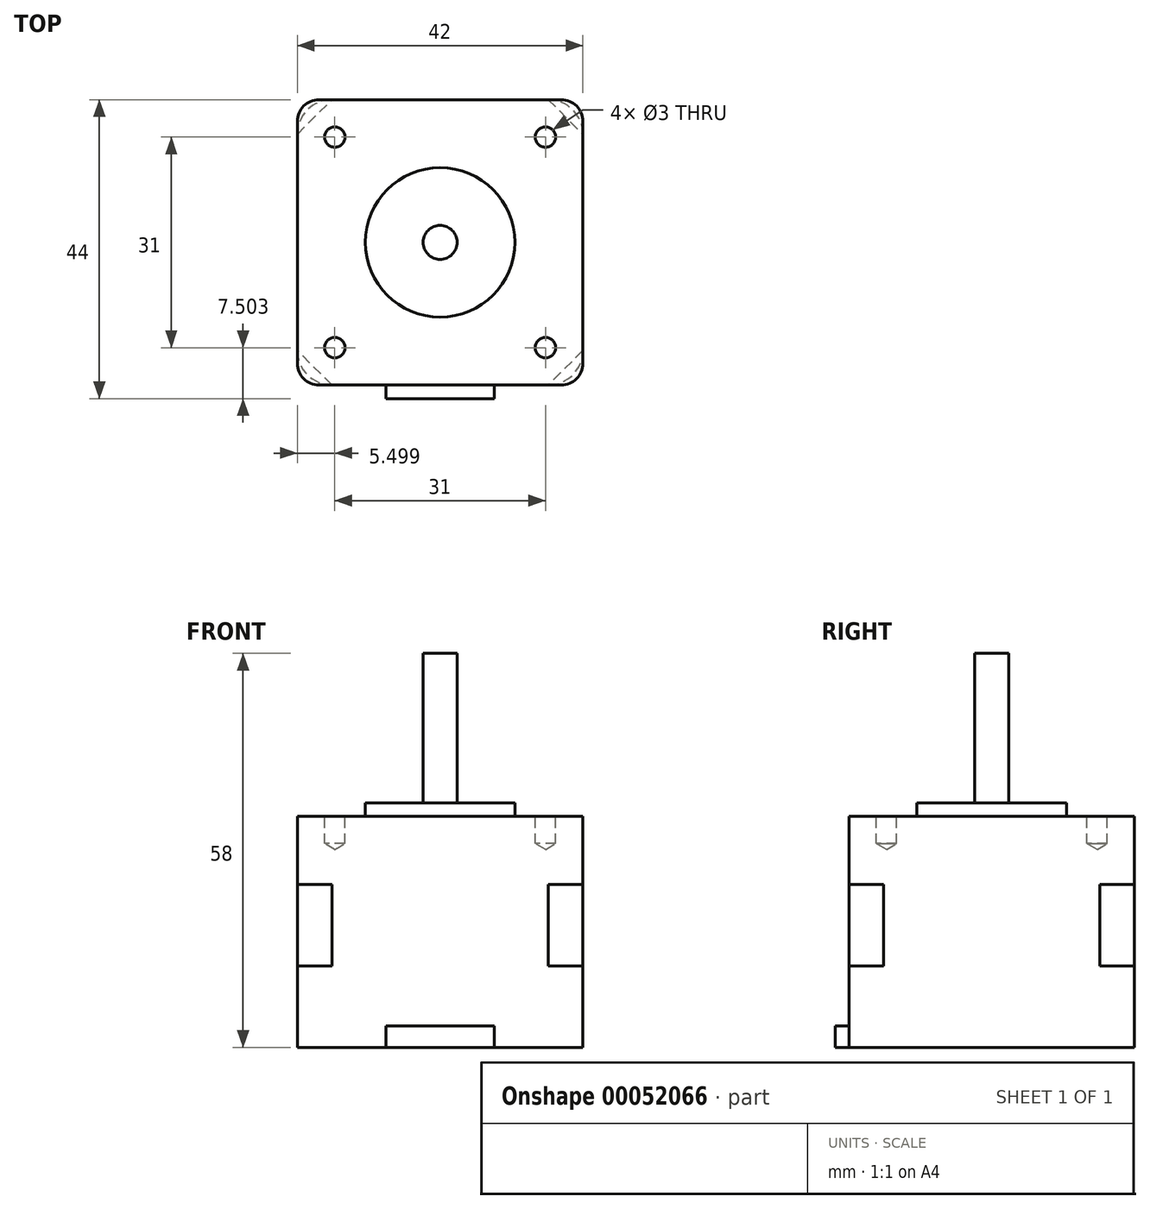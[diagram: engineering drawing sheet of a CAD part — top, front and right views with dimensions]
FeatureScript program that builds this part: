
annotation { "Feature Type Name" : "Feature", "Feature Type Description" : "" }
export const myFeature = defineFeature(function(context is Context, id is Id, definition is map)
    precondition{}
    {
        {
            var Q0;
            Q0=qCreatedBy(makeId("Top.planeOp"),FACE);
            var sketch = newSketch(context, id + "F0", { "sketchPlane" : qUnion([Q0])});
            skLineSegment(sketch, "E0.bottom", {"start": v(-20.04, 16.68) * mm, "end": v(21.96, 16.68) * mm});
            skLineSegment(sketch, "E0.top", {"start": v(-20.04, -25.32) * mm, "end": v(21.96, -25.32) * mm});
            skLineSegment(sketch, "E0.left", {"start": v(-20.04, 16.68) * mm, "end": v(-20.04, -25.32) * mm});
            skLineSegment(sketch, "E0.right", {"start": v(21.96, 16.68) * mm, "end": v(21.96, -25.32) * mm});
            skSolve(sketch);
        }
        {
            var Q0;
            Q0=makeQuery(id+"F0.imprint","IMPRINT",FACE,{"disambiguationData":[TD([[makeQuery(id+"F0.imprint","IMPRINT",EDGE,{"derivedFrom":sQuery(id+"F0.wireOp",EDGE,"E0.bottom")}),-1.0]])]});
            extrude(context, id + "F1", {"entities" : qUnion([Q0]), "depth" : 10 * mm});
        }
        {
            var Q0;
            Q0=makeQuery(id+"F1.opExtrude","CAP_FACE",FACE,{"disambiguationData":[OSD([sQuery(id+"F0.wireOp",EDGE,"E0.bottom"),sQuery(id+"F0.wireOp",EDGE,"E0.top"),sQuery(id+"F0.wireOp",EDGE,"E0.left"),sQuery(id+"F0.wireOp",EDGE,"E0.right")])],"isStart":false});
            var sketch = newSketch(context, id + "F2", { "sketchPlane" : qUnion([Q0])});
            skLineSegment(sketch, "E1", {"start": v(-20.04, 16.68) * mm, "end": v(21.96, -25.32) * mm, "construction": true});
            skLineSegment(sketch, "E2", {"start": v(21.96, 16.68) * mm, "end": v(-20.04, -25.32) * mm, "construction": true});
            skCircle(sketch, "E3", {"center": v(0.96, -4.32) * mm, "radius": 11 * mm});
            skSolve(sketch);
        }
        {
            var Q0;
            Q0=makeQuery(id+"F2.imprint","IMPRINT",FACE,{"disambiguationData":[TD([[makeQuery(id+"F2.imprint","IMPRINT",EDGE,{"derivedFrom":sQuery(id+"F2.wireOp",EDGE,"E3")}),1.0]])]});
            extrude(context, id + "F3", {"entities" : qUnion([Q0]), "operationType" : NewBodyOperationType.ADD, "depth" : 2 * mm});
        }
        {
            var Q0;
            Q0=makeQuery(id+"F1.opExtrude","SWEPT_EDGE",EDGE,{"disambiguationData":[OSD([sQuery(id+"F0.wireOp",EDGE,"E0.top"),sQuery(id+"F0.wireOp",EDGE,"E0.right")])]});
            var Q1;
            Q1=makeQuery(id+"F1.opExtrude","SWEPT_EDGE",EDGE,{"disambiguationData":[OSD([sQuery(id+"F0.wireOp",EDGE,"E0.bottom"),sQuery(id+"F0.wireOp",EDGE,"E0.right")])]});
            var Q2;
            Q2=makeQuery(id+"F1.opExtrude","SWEPT_EDGE",EDGE,{"disambiguationData":[OSD([sQuery(id+"F0.wireOp",EDGE,"E0.bottom"),sQuery(id+"F0.wireOp",EDGE,"E0.left")])]});
            var Q3;
            Q3=makeQuery(id+"F1.opExtrude","SWEPT_EDGE",EDGE,{"disambiguationData":[OSD([sQuery(id+"F0.wireOp",EDGE,"E0.top"),sQuery(id+"F0.wireOp",EDGE,"E0.left")])]});
            fillet(context, id + "F4", {"entities" : qUnion([Q0, Q1, Q2, Q3]), "radius" : 3.17 * mm, "tangentPropagation" : true, "allowEdgeOverflow" : false});
        }
        {
            var Q0;
            Q0=makeQuery(id+"F1.opExtrude","CAP_FACE",FACE,{"disambiguationData":[OSD([sQuery(id+"F0.wireOp",EDGE,"E0.bottom"),sQuery(id+"F0.wireOp",EDGE,"E0.top"),sQuery(id+"F0.wireOp",EDGE,"E0.left"),sQuery(id+"F0.wireOp",EDGE,"E0.right")])],"isStart":true});
            var sketch = newSketch(context, id + "F5", { "sketchPlane" : qUnion([Q0])});
            skLineSegment(sketch, "E4", {"start": v(-20.04, -11.6) * mm, "end": v(-20.04, 20.24) * mm});
            skLineSegment(sketch, "E5", {"start": v(0.96, 25.32) * mm, "end": v(0.96, -16.68) * mm, "construction": true});
            skLineSegment(sketch, "E6", {"start": v(-14.96, 25.32) * mm, "end": v(0.96, 25.32) * mm});
            skLineSegment(sketch, "E7", {"start": v(-14.96, -16.68) * mm, "end": v(0.96, -16.68) * mm});
            skLineSegment(sketch, "E8.MirrorCS", {"start": v(16.88, 25.32) * mm, "end": v(0.96, 25.32) * mm});
            skLineSegment(sketch, "E9.MirrorCS", {"start": v(21.96, -11.6) * mm, "end": v(21.96, 20.24) * mm});
            skLineSegment(sketch, "E10.MirrorCS", {"start": v(16.88, -16.68) * mm, "end": v(0.96, -16.68) * mm});
            skLineSegment(sketch, "E11.top", {"start": v(-20.04, 20.24) * mm, "end": v(-14.96, 20.24) * mm, "construction": true});
            skLineSegment(sketch, "E11.right", {"start": v(-14.96, 25.32) * mm, "end": v(-14.96, 20.24) * mm, "construction": true});
            skLineSegment(sketch, "E12", {"start": v(-14.96, 25.32) * mm, "end": v(-20.04, 20.24) * mm});
            skPoint(sketch, "E13.orphan", {"position": v(-20.04, 25.32) * mm});
            skLineSegment(sketch, "E14.1.0", {"start": v(-20.04, -11.6) * mm, "end": v(-14.96, -16.68) * mm});
            skLineSegment(sketch, "E14.2.0", {"start": v(16.88, -16.68) * mm, "end": v(21.96, -11.6) * mm});
            skLineSegment(sketch, "E14.3.0", {"start": v(21.96, 20.24) * mm, "end": v(16.88, 25.32) * mm});
            skPoint(sketch, "E14.center", {"position": v(0.96, 4.32) * mm});
            skPoint(sketch, "E15.orphan", {"position": v(21.96, 25.32) * mm});
            skPoint(sketch, "E16.orphan", {"position": v(21.96, -16.68) * mm});
            skPoint(sketch, "E17.orphan", {"position": v(-20.04, -16.68) * mm});
            skSolve(sketch);
        }
        {
            var Q0;
            Q0=qSketchRegion(id+"F5",true);
            extrude(context, id + "F6", {"entities" : qUnion([Q0]), "operationType" : NewBodyOperationType.ADD, "depth" : 12 * mm});
        }
        {
            var Q0;
            Q0=makeQuery(id+"F6.opExtrude","CAP_FACE",FACE,{"disambiguationData":[OSD([sQuery(id+"F5.wireOp",EDGE,"E4"),sQuery(id+"F5.wireOp",EDGE,"E6"),sQuery(id+"F5.wireOp",EDGE,"E7"),sQuery(id+"F5.wireOp",EDGE,"E8.MirrorCS"),sQuery(id+"F5.wireOp",EDGE,"E9.MirrorCS"),sQuery(id+"F5.wireOp",EDGE,"E10.MirrorCS"),sQuery(id+"F5.wireOp",EDGE,"E12"),sQuery(id+"F5.wireOp",EDGE,"E14.1.0"),sQuery(id+"F5.wireOp",EDGE,"E14.2.0"),sQuery(id+"F5.wireOp",EDGE,"E14.3.0")])],"isStart":false});
            var sketch = newSketch(context, id + "F7", { "sketchPlane" : qUnion([Q0])});
            skLineSegment(sketch, "E18.bottom", {"start": v(-20.04, 25.32) * mm, "end": v(21.96, 25.32) * mm});
            skLineSegment(sketch, "E18.top", {"start": v(-20.04, -16.68) * mm, "end": v(21.96, -16.68) * mm});
            skLineSegment(sketch, "E18.left", {"start": v(-20.04, 25.32) * mm, "end": v(-20.04, -16.68) * mm});
            skLineSegment(sketch, "E18.right", {"start": v(21.96, 25.32) * mm, "end": v(21.96, -16.68) * mm});
            skSolve(sketch);
        }
        {
            var Q0;
            Q0=qSketchRegion(id+"F7",true);
            extrude(context, id + "F8", {"entities" : qUnion([Q0]), "operationType" : NewBodyOperationType.ADD, "depth" : 12 * mm});
        }
        {
            var Q0;
            Q0=makeQuery(id+"F8.opExtrude","SWEPT_EDGE",EDGE,{"disambiguationData":[OSD([sQuery(id+"F7.wireOp",EDGE,"E18.top"),sQuery(id+"F7.wireOp",EDGE,"E18.right")])]});
            var Q1;
            Q1=makeQuery(id+"F8.opExtrude","SWEPT_EDGE",EDGE,{"disambiguationData":[OSD([sQuery(id+"F7.wireOp",EDGE,"E18.bottom"),sQuery(id+"F7.wireOp",EDGE,"E18.right")])]});
            var Q2;
            Q2=makeQuery(id+"F8.opExtrude","SWEPT_EDGE",EDGE,{"disambiguationData":[OSD([sQuery(id+"F7.wireOp",EDGE,"E18.top"),sQuery(id+"F7.wireOp",EDGE,"E18.left")])]});
            var Q3;
            Q3=makeQuery(id+"F8.opExtrude","SWEPT_EDGE",EDGE,{"disambiguationData":[OSD([sQuery(id+"F7.wireOp",EDGE,"E18.bottom"),sQuery(id+"F7.wireOp",EDGE,"E18.left")])]});
            fillet(context, id + "F9", {"entities" : qUnion([Q0, Q1, Q2, Q3]), "radius" : 5.08 * mm, "tangentPropagation" : true, "allowEdgeOverflow" : false});
        }
        {
            var Q0;
            Q0=makeQuery(id+"F1.opExtrude","CAP_FACE",FACE,{"disambiguationData":[OSD([sQuery(id+"F0.wireOp",EDGE,"E0.bottom"),sQuery(id+"F0.wireOp",EDGE,"E0.top"),sQuery(id+"F0.wireOp",EDGE,"E0.left"),sQuery(id+"F0.wireOp",EDGE,"E0.right")])],"isStart":false});
            var sketch = newSketch(context, id + "F10", { "sketchPlane" : qUnion([Q0])});
            skLineSegment(sketch, "E19.bottom", {"start": v(0.96, -4.32) * mm, "end": v(-14.54, -4.32) * mm, "construction": true});
            skLineSegment(sketch, "E19.top", {"start": v(0.96, 11.18) * mm, "end": v(-14.54, 11.18) * mm, "construction": true});
            skLineSegment(sketch, "E19.left", {"start": v(0.96, -4.32) * mm, "end": v(0.96, 11.18) * mm, "construction": true});
            skLineSegment(sketch, "E19.right", {"start": v(-14.54, -4.32) * mm, "end": v(-14.54, 11.18) * mm, "construction": true});
            skCircle(sketch, "E20", {"center": v(-14.54, 11.18) * mm, "radius": 1.5 * mm});
            skCircle(sketch, "E21.0.1.0", {"center": v(-14.54, -19.82) * mm, "radius": 1.5 * mm});
            skCircle(sketch, "E21.1.0.0", {"center": v(16.46, 11.18) * mm, "radius": 1.5 * mm});
            skCircle(sketch, "E21.1.1.0", {"center": v(16.46, -19.82) * mm, "radius": 1.5 * mm});
            skLineSegment(sketch, "E21.direction1", {"start": v(-14.54, 11.18) * mm, "end": v(16.46, 11.18) * mm, "construction": true});
            skLineSegment(sketch, "E21.direction2", {"start": v(-14.54, 11.18) * mm, "end": v(-14.54, -19.82) * mm, "construction": true});
            skSolve(sketch);
        }
        {
            var Q0;
            Q0=sQuery(id+"F10.wireOp",VERTEX,"E20.center");
            var Q1;
            Q1=sQuery(id+"F10.wireOp",VERTEX,"E21.direction2.end");
            var Q2;
            Q2=sQuery(id+"F10.wireOp",VERTEX,"E21.1.1.0.center");
            var Q3;
            Q3=sQuery(id+"F10.wireOp",VERTEX,"E21.direction1.end");
            var Q4;
            Q4=makeQuery(id+"F1.opExtrude","SWEPT_BODY",BODY,{"disambiguationData":[OSD([sQuery(id+"F0.wireOp",EDGE,"E0.bottom"),sQuery(id+"F0.wireOp",EDGE,"E0.top"),sQuery(id+"F0.wireOp",EDGE,"E0.left"),sQuery(id+"F0.wireOp",EDGE,"E0.right")])]});
            hole(context, id + "F11", {"style" : HoleStyle.SIMPLE, "holeDiameter" : 3 * mm, "endStyle" : HoleEndStyle.BLIND, "holeDepth" : 4 * mm, "locations" : qUnion([Q0, Q1, Q2, Q3]), "scope" : qUnion([Q4])});
        }
        {
            var Q0;
            Q0=makeQuery(id+"F3.opExtrude","CAP_FACE",FACE,{"disambiguationData":[OSD([sQuery(id+"F2.wireOp",EDGE,"E3")])],"isStart":false});
            var sketch = newSketch(context, id + "F12", { "sketchPlane" : qUnion([Q0])});
            skCircle(sketch, "E22", {"center": v(0.96, -4.32) * mm, "radius": 2.5 * mm});
            skSolve(sketch);
        }
        {
            var Q0;
            Q0=qSketchRegion(id+"F12",true);
            extrude(context, id + "F13", {"entities" : qUnion([Q0]), "operationType" : NewBodyOperationType.ADD, "depth" : 22 * mm});
        }
        {
            var Q0;
            Q0=makeQuery(id+"F8.boolean.opBoolean","MERGE",FACE,{"derivedFrom":[makeQuery(id+"F6.boolean.opBoolean","MERGE",FACE,{"derivedFrom":[makeQuery(id+"F1.opExtrude","SWEPT_FACE",FACE,{"disambiguationData":[OSD([sQuery(id+"F0.wireOp",EDGE,"E0.top")])]}),makeQuery(id+"F6.opExtrude","SWEPT_FACE",FACE,{"disambiguationData":[OSD([sQuery(id+"F5.wireOp",EDGE,"E6"),sQuery(id+"F5.wireOp",EDGE,"E8.MirrorCS")])]})]}),makeQuery(id+"F8.opExtrude","SWEPT_FACE",FACE,{"disambiguationData":[OSD([sQuery(id+"F7.wireOp",EDGE,"E18.bottom")])]})]});
            var sketch = newSketch(context, id + "F14", { "sketchPlane" : qUnion([Q0])});
            skLineSegment(sketch, "E23.bottom", {"start": v(0.96, -24) * mm, "end": v(8.9, -24) * mm});
            skLineSegment(sketch, "E23.top", {"start": v(0.96, -20.88) * mm, "end": v(8.9, -20.88) * mm});
            skLineSegment(sketch, "E23.left", {"start": v(0.96, -24) * mm, "end": v(0.96, -20.88) * mm, "construction": true});
            skLineSegment(sketch, "E23.right", {"start": v(8.9, -24) * mm, "end": v(8.9, -20.88) * mm});
            skLineSegment(sketch, "E24.MirrorCS", {"start": v(0.96, -20.88) * mm, "end": v(-6.99, -20.88) * mm});
            skLineSegment(sketch, "E25.MirrorCS", {"start": v(-6.99, -24) * mm, "end": v(-6.99, -20.88) * mm});
            skLineSegment(sketch, "E26.MirrorCS", {"start": v(0.96, -24) * mm, "end": v(-6.99, -24) * mm});
            skSolve(sketch);
        }
        {
            var Q0;
            Q0=makeQuery(id+"F14.imprint","IMPRINT",FACE,{"disambiguationData":[TD([[makeQuery(id+"F14.imprint","IMPRINT",EDGE,{"derivedFrom":sQuery(id+"F14.wireOp",EDGE,"E23.bottom")}),1.0]])]});
            var Q1;
            Q1=sQuery(id+"F14.wireOp",EDGE,"E23.bottom");
            var Q2;
            Q2=sQuery(id+"F14.wireOp",EDGE,"E26.MirrorCS");
            var Q3;
            Q3=sQuery(id+"F14.wireOp",EDGE,"E25.MirrorCS");
            var Q4;
            Q4=sQuery(id+"F14.wireOp",EDGE,"E24.MirrorCS");
            var Q5;
            Q5=sQuery(id+"F14.wireOp",EDGE,"E23.top");
            var Q6;
            Q6=sQuery(id+"F14.wireOp",EDGE,"E23.right");
            extrude(context, id + "F15", {"entities" : qUnion([Q0]), "operationType" : NewBodyOperationType.ADD, "surfaceEntities" : qUnion([Q1, Q2, Q3, Q4, Q5, Q6]), "depth" : 2 * mm});
        }
    });
